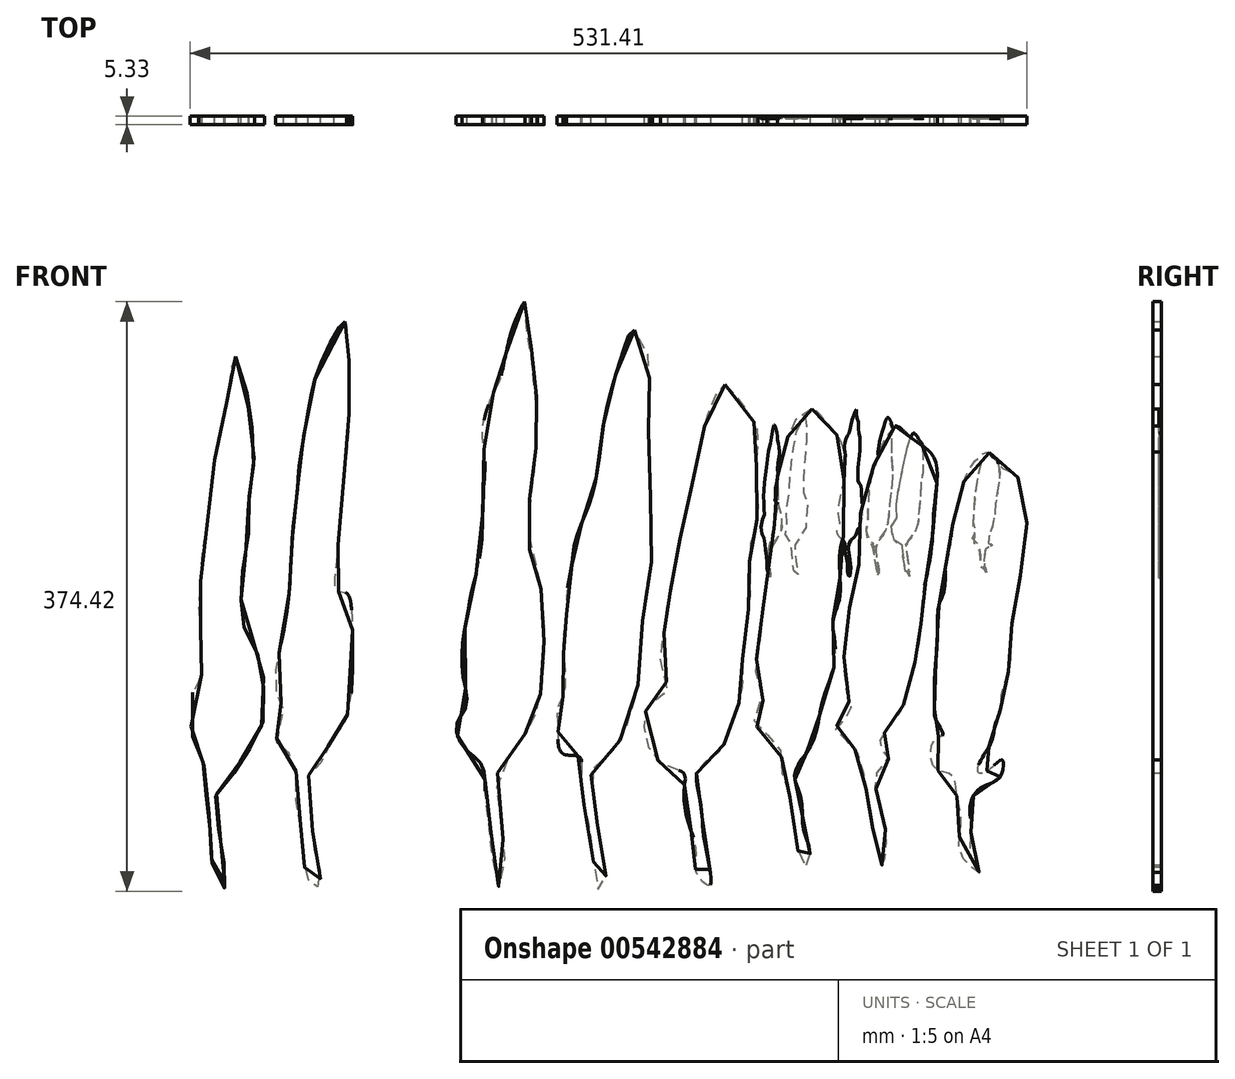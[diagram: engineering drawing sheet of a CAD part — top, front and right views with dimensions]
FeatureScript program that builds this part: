
annotation { "Feature Type Name" : "Feature", "Feature Type Description" : "" }
export const myFeature = defineFeature(function(context is Context, id is Id, definition is map)
    precondition{}
    {
        {
            var Q0;
            Q0=qCreatedBy(makeId("Front.planeOp"),FACE);
            var sketch = newSketch(context, id + "F0", { "sketchPlane" : qUnion([Q0])});
            skFitSpline(sketch, "E0", {"points": [v(-26.75, 46.41) * mm, v(-26.5, 43.12) * mm, v(-26, 39.07) * mm, v(-26, 32.23) * mm, v(-26.25, 24.64) * mm, v(-27.51, 13) * mm, v(-28.33, 2.5) * mm, v(-28.33, -2.36) * mm, v(-26.56, -2.8) * mm, v(-25.46, -7.65) * mm, v(-26.25, -24.73) * mm, v(-28.52, -28.78) * mm, v(-29.8, -30.55) * mm, v(-30.55, -33.08) * mm, v(-33.08, -35.36) * mm, v(-32.83, -41.7) * mm, v(-32.32, -49.5) * mm, v(-31.2, -54.37) * mm, v(-32.07, -56.37) * mm, v(-33.62, -54.37) * mm, v(-34.3, -49.5) * mm, v(-34.72, -45.33) * mm, v(-35.61, -40.17) * mm, v(-36.26, -32.55) * mm, v(-38.9, -30.55) * mm, v(-38.46, -26.6) * mm, v(-37.9, -23.97) * mm, v(-39.16, -20.94) * mm, v(-38.69, -13.6) * mm, v(-37.14, -5.44) * mm, v(-36.48, 4.03) * mm, v(-36.04, 9.98) * mm, v(-35.38, 15.94) * mm, v(-34.94, 21.22) * mm, v(-33.59, 29.2) * mm, v(-31.56, 37.8) * mm, v(-26.75, 46.41) * mm]});
            skFitSpline(sketch, "E1", {"points": [v(-8.5, 48.51) * mm, v(-7.65, 45.54) * mm, v(-7.65, 41.3) * mm, v(-7.65, 37.26) * mm, v(-7.86, 34.07) * mm, v(-8.29, 28.97) * mm, v(-8.71, 24.09) * mm, v(-9.35, 21.33) * mm, v(-9.14, 17.5) * mm, v(-9.77, 12.62) * mm, v(-8.71, 6.89) * mm, v(-7.65, 3.27) * mm, v(-7.44, -2.25) * mm, v(-6.8, -4.8) * mm, v(-6.8, -7.77) * mm, v(-7.22, -10.32) * mm, v(-7.86, -15) * mm, v(-8.29, -19.66) * mm, v(-9.99, -23.7) * mm, v(-11.47, -26.67) * mm, v(-12.32, -29.64) * mm, v(-15.08, -31.98) * mm, v(-16.14, -33.9) * mm, v(-16.14, -38.14) * mm, v(-15.72, -43.24) * mm, v(-15.08, -45.79) * mm, v(-14.45, -50.03) * mm, v(-14.02, -54.7) * mm, v(-14.66, -56.2) * mm, v(-15.72, -54.7) * mm, v(-16.36, -52.16) * mm, v(-16.78, -48.76) * mm, v(-17.63, -44.72) * mm, v(-18.06, -40.05) * mm, v(-18.48, -35.6) * mm, v(-19.33, -33.47) * mm, v(-22.1, -32.4) * mm, v(-23.58, -29.64) * mm, v(-23.15, -27.1) * mm, v(-22.1, -23.91) * mm, v(-22.1, -23.91) * mm, v(-21.24, -20.94) * mm, v(-22.1, -18.39) * mm, v(-22.73, -14.57) * mm, v(-22.73, -10.53) * mm, v(-22.1, -7.56) * mm, v(-21.67, -4.37) * mm, v(-21.45, 0) * mm, v(-21.03, 2.85) * mm, v(-20.18, 5.19) * mm, v(-18.48, 7.52) * mm, v(-18.48, 11.35) * mm, v(-17.84, 17.08) * mm, v(-17.2, 22.39) * mm, v(-16.57, 27.27) * mm, v(-15.72, 31.73) * mm, v(-14.87, 35.56) * mm, v(-13.6, 41.08) * mm, v(-11.68, 43.63) * mm, v(-10.4, 46.39) * mm, v(-8.5, 48.51) * mm]});
            skFitSpline(sketch, "E2", {"points": [v(-46.56, 40.04) * mm, v(-47.72, 35.4) * mm, v(-48.19, 31.7) * mm, v(-49.35, 26.59) * mm, v(-50.74, 18.7) * mm, v(-51.43, 11.74) * mm, v(-52.6, 5.25) * mm, v(-53.06, -1.94) * mm, v(-53.29, -5.88) * mm, v(-52.83, -10.3) * mm, v(-52.83, -14.47) * mm, v(-52.83, -17.95) * mm, v(-54.45, -21.2) * mm, v(-54.45, -28.59) * mm, v(-53.75, -30.24) * mm, v(-52.36, -33.95) * mm, v(-52.13, -37.66) * mm, v(-51.43, -42.53) * mm, v(-51.2, -46.47) * mm, v(-50.97, -50.65) * mm, v(-50.04, -54.82) * mm, v(-48.65, -56.45) * mm, v(-48.65, -54.13) * mm, v(-48.65, -51.58) * mm, v(-49.35, -47.63) * mm, v(-50.04, -43) * mm, v(-50.04, -39.28) * mm, v(-47.26, -36.5) * mm, v(-46.56, -34.65) * mm, v(-44.48, -31.86) * mm, v(-43.08, -29.08) * mm, v(-41.46, -25.83) * mm, v(-41.46, -21.89) * mm, v(-41.7, -16.55) * mm, v(-42.85, -13.07) * mm, v(-44.24, -9.6) * mm, v(-45.87, -8.44) * mm, v(-45.64, -4.72) * mm, v(-45.64, -1.7) * mm, v(-45.17, 2.23) * mm, v(-44.24, 7.57) * mm, v(-44.24, 11.98) * mm, v(-43.78, 17.77) * mm, v(-43.32, 20.33) * mm, v(-43.32, 25.43) * mm, v(-44.24, 30.53) * mm, v(-44.7, 35.17) * mm, v(-46.56, 40.04) * mm]});
            skFitSpline(sketch, "E3", {"points": [v(5.86, 50.01) * mm, v(5.86, 46.07) * mm, v(7.02, 42.13) * mm, v(7.02, 39.58) * mm, v(7.25, 35.87) * mm, v(8.18, 31.46) * mm, v(7.94, 27.52) * mm, v(7.94, 22.88) * mm, v(7.48, 18.47) * mm, v(6.78, 14.3) * mm, v(6.78, 9.89) * mm, v(6.78, 5.71) * mm, v(7.02, 3.63) * mm, v(8.4, 2.23) * mm, v(8.87, -2.4) * mm, v(9.33, -7.28) * mm, v(9.33, -11.22) * mm, v(9.33, -16.55) * mm, v(8.87, -20.03) * mm, v(7.94, -24.67) * mm, v(6.55, -26.3) * mm, v(5.86, -28.85) * mm, v(4.26, -31.3) * mm, v(1.32, -34.23) * mm, v(1.32, -43.58) * mm, v(1.94, -47.7) * mm, v(2.19, -52.4) * mm, v(1.32, -56.2) * mm, v(0, -52.4) * mm, v(0, -47.73) * mm, v(-1.22, -41.85) * mm, v(-1.35, -38.4) * mm, v(-1.95, -33.98) * mm, v(-5.05, -31) * mm, v(-6.5, -26.7) * mm, v(-4.8, -23.57) * mm, v(-5.22, -18.4) * mm, v(-5.45, -12.36) * mm, v(-4.55, -6.99) * mm, v(-3.66, -2.06) * mm, v(-2.54, 2.19) * mm, v(-1.87, 7.78) * mm, v(-1.62, 15.25) * mm, v(-1.37, 22.42) * mm, v(-1.8, 26.67) * mm, v(0, 33.06) * mm, v(1.32, 35.66) * mm, v(1.71, 37.09) * mm, v(2.38, 40.22) * mm, v(3.5, 44.7) * mm, v(5.86, 50.01) * mm]});
            skFitSpline(sketch, "E4", {"points": [v(-62.57, -56) * mm, v(-62.87, -50.88) * mm, v(-63.77, -44.86) * mm, v(-64.98, -39.44) * mm, v(-65.88, -34.31) * mm, v(-66.18, -27.38) * mm, v(-66.78, -19.55) * mm, v(-66.48, -14.73) * mm, v(-66.18, -8.1) * mm, v(-65.58, -2.37) * mm, v(-64.67, 3.95) * mm, v(-63.47, 10.58) * mm, v(-62.26, 15.1) * mm, v(-60.46, 18.72) * mm, v(-59.25, 15.1) * mm, v(-58.65, 10.28) * mm, v(-58.35, 2.75) * mm, v(-58.95, -3.28) * mm, v(-59.25, -10.2) * mm, v(-59.25, -15.63) * mm, v(-59.85, -19.55) * mm, v(-57.74, -24.37) * mm, v(-57.74, -28.59) * mm, v(-57.74, -28.59) * mm, v(-57.14, -34.31) * mm, v(-59.85, -38.83) * mm, v(-61.96, -42.75) * mm, v(-61.06, -51.19) * mm, v(-62.57, -56) * mm]});
            skFitSpline(sketch, "E5", {"points": [v(25.76, 44.9) * mm, v(23.67, 40.98) * mm, v(22.1, 35.74) * mm, v(20.52, 29.72) * mm, v(19.74, 24.48) * mm, v(18.95, 18.72) * mm, v(17.64, 13.49) * mm, v(16.07, 9.56) * mm, v(14.76, 5.37) * mm, v(14.5, 2.75) * mm, v(13.45, -3.27) * mm, v(13.45, -7.2) * mm, v(12.93, -10.34) * mm, v(12.93, -13.49) * mm, v(13.2, -17.94) * mm, v(12.93, -21.34) * mm, v(11.88, -23.44) * mm, v(11.88, -26.58) * mm, v(11.88, -29.46) * mm, v(12.93, -32.08) * mm, v(15.8, -32.6) * mm, v(16.07, -37.31) * mm, v(17.12, -43.34) * mm, v(18.17, -49.62) * mm, v(19.48, -56.95) * mm, v(20.52, -54.86) * mm, v(20, -50.4) * mm, v(18.95, -44.12) * mm, v(18.17, -38.1) * mm, v(18.17, -34.96) * mm, v(21.3, -32.08) * mm, v(24.19, -27.36) * mm, v(26.28, -20.3) * mm, v(27.07, -10.87) * mm, v(27.6, -4.58) * mm, v(28.9, 3.27) * mm, v(28.9, 10.87) * mm, v(28.38, 22.13) * mm, v(28.38, 28.67) * mm, v(28.38, 34.7) * mm, v(28.38, 39.93) * mm, v(25.76, 44.9) * mm]});
            skFitSpline(sketch, "E6", {"points": [v(42.26, 34.96) * mm, v(45.14, 31.55) * mm, v(48.02, 27.1) * mm, v(48.02, 23.17) * mm, v(48.02, 16.1) * mm, v(48.02, 10.34) * mm, v(46.7, 5.37) * mm, v(46.7, 2.23) * mm, v(46.7, -3.54) * mm, v(46.19, -7.72) * mm, v(45.4, -14.27) * mm, v(45.4, -18.98) * mm, v(44.61, -23.17) * mm, v(43.57, -26.32) * mm, v(41.2, -31.55) * mm, v(37.8, -34.17) * mm, v(37.02, -36.27) * mm, v(37.8, -41.24) * mm, v(38.33, -46.74) * mm, v(39.38, -52.5) * mm, v(39.38, -55.9) * mm, v(37.02, -53.55) * mm, v(37.02, -50.4) * mm, v(36.23, -46.48) * mm, v(34.93, -41.77) * mm, v(34.93, -37.31) * mm, v(34.66, -35.48) * mm, v(29.95, -33.12) * mm, v(27.6, -26.84) * mm, v(28.64, -22.91) * mm, v(31.78, -20.56) * mm, v(30.74, -16.63) * mm, v(31, -10.87) * mm, v(31.78, -5.1) * mm, v(32.3, -2.49) * mm, v(33.35, 3.27) * mm, v(34.66, 9.82) * mm, v(36.23, 16.89) * mm, v(38.07, 25.53) * mm, v(39.64, 31.03) * mm, v(42.26, 34.96) * mm]});
            skFitSpline(sketch, "E7", {"points": [v(90.18, 22.65) * mm, v(92.27, 20.03) * mm, v(95.15, 18.46) * mm, v(95.94, 14.8) * mm, v(96.99, 9.56) * mm, v(96.2, 3.54) * mm, v(95.41, -2.75) * mm, v(94.37, -7.72) * mm, v(94.1, -11.4) * mm, v(93.58, -17.41) * mm, v(92.27, -21.34) * mm, v(92.27, -23.7) * mm, v(91.22, -26.84) * mm, v(90.7, -29.46) * mm, v(88.08, -34.43) * mm, v(88.34, -35.48) * mm, v(90.7, -34.43) * mm, v(92.53, -33.12) * mm, v(92.27, -36) * mm, v(89.92, -37.58) * mm, v(88.08, -38.62) * mm, v(86.77, -40.98) * mm, v(86.77, -44.12) * mm, v(86.77, -47) * mm, v(87.03, -51.45) * mm, v(88.34, -53.55) * mm, v(85.17, -50.6) * mm, v(84.94, -45.96) * mm, v(84.94, -42.45) * mm, v(84.15, -38.62) * mm, v(83.63, -36) * mm, v(80.75, -34.96) * mm, v(79.44, -32.08) * mm, v(80.75, -28.94) * mm, v(81.8, -28.67) * mm, v(80.49, -25.8) * mm, v(80.23, -23.2) * mm, v(80.23, -17.94) * mm, v(80.75, -11.91) * mm, v(81.01, -5.1) * mm, v(82.06, -2.23) * mm, v(82.32, 2.49) * mm, v(83.37, 6.68) * mm, v(83.63, 9.82) * mm, v(84.68, 13.75) * mm, v(85.73, 17.94) * mm, v(88.08, 21.6) * mm, v(90.18, 22.65) * mm]});
            skFitSpline(sketch, "E8", {"points": [v(57.98, 30.54) * mm, v(54.5, 27.83) * mm, v(53.34, 23.96) * mm, v(51.8, 18.55) * mm, v(51.8, 12.37) * mm, v(49.86, 4.25) * mm, v(50.25, 1.93) * mm, v(49.47, -2.32) * mm, v(48.7, -10.44) * mm, v(47.93, -18.55) * mm, v(49.09, -22.42) * mm, v(47.93, -23.58) * mm, v(47.93, -27.06) * mm, v(51.8, -30.15) * mm, v(52.57, -35.56) * mm, v(54.11, -40.2) * mm, v(55.27, -49.09) * mm, v(57.2, -52.57) * mm, v(57.6, -49.47) * mm, v(56.43, -45.6) * mm, v(56.04, -40.2) * mm, v(54.88, -36.72) * mm, v(55.27, -34.4) * mm, v(56.82, -32.08) * mm, v(58.75, -28.22) * mm, v(59.9, -22.42) * mm, v(62.23, -14.69) * mm, v(61.84, -7.72) * mm, v(63, -3.87) * mm, v(63, 3.87) * mm, v(63.77, 8.5) * mm, v(63.77, 17.78) * mm, v(63.39, 24.35) * mm, v(59.9, 28.99) * mm, v(57.98, 30.54) * mm]});
            skFitSpline(sketch, "E9", {"points": [v(73.05, 27.44) * mm, v(69.57, 21.26) * mm, v(66.87, 11.98) * mm, v(66.48, 2.32) * mm, v(64.93, -5.02) * mm, v(63.77, -13.91) * mm, v(64.55, -22.03) * mm, v(64.93, -24.74) * mm, v(62.23, -27.44) * mm, v(64.93, -30.15) * mm, v(67.25, -35.17) * mm, v(68.41, -42.13) * mm, v(69.57, -48.32) * mm, v(70.73, -52.18) * mm, v(71.5, -47.54) * mm, v(70.35, -41.74) * mm, v(69.96, -35.17) * mm, v(71.9, -32.85) * mm, v(70.35, -30.54) * mm, v(72.66, -26.28) * mm, v(74.6, -23.2) * mm, v(76.53, -16.23) * mm, v(77.69, -10.44) * mm, v(78.08, -3.87) * mm, v(79.62, 4.64) * mm, v(80.23, 13.14) * mm, v(80.23, 21.65) * mm, v(75.76, 25.51) * mm, v(73.05, 27.44) * mm]});
            skSolve(sketch);
        }
        {
            var Q0;
            Q0=qSketchRegion(id+"F0",true);
            extrude(context, id + "F1", {"entities" : qUnion([Q0]), "depth" : 1.52 * mm, "offsetDistance" : 25.4 * mm});
        }
        {
            var Q0;
            Q0=makeQuery(id+"F1.opExtrude","SWEPT_BODY",BODY,{"disambiguationData":[OSD([sQuery(id+"F0.wireOp",EDGE,"E4")])]});
            var Q1;
            Q1=makeQuery(id+"F1.opExtrude","SWEPT_BODY",BODY,{"disambiguationData":[OSD([sQuery(id+"F0.wireOp",EDGE,"E2")])]});
            var Q2;
            Q2=makeQuery(id+"F1.opExtrude","SWEPT_BODY",BODY,{"disambiguationData":[OSD([sQuery(id+"F0.wireOp",EDGE,"E1")])]});
            var Q3;
            Q3=makeQuery(id+"F1.opExtrude","SWEPT_BODY",BODY,{"disambiguationData":[OSD([sQuery(id+"F0.wireOp",EDGE,"E0")])]});
            var Q4;
            Q4=makeQuery(id+"F1.opExtrude","SWEPT_BODY",BODY,{"disambiguationData":[OSD([sQuery(id+"F0.wireOp",EDGE,"E3")])]});
            var Q5;
            Q5=makeQuery(id+"F1.opExtrude","SWEPT_BODY",BODY,{"disambiguationData":[OSD([sQuery(id+"F0.wireOp",EDGE,"E5")])]});
            var Q6;
            Q6=makeQuery(id+"F1.opExtrude","SWEPT_BODY",BODY,{"disambiguationData":[OSD([sQuery(id+"F0.wireOp",EDGE,"E6")])]});
            var Q7;
            Q7=makeQuery(id+"F1.opExtrude","SWEPT_BODY",BODY,{"disambiguationData":[OSD([sQuery(id+"F0.wireOp",EDGE,"E8")])]});
            var Q8;
            Q8=makeQuery(id+"F1.opExtrude","SWEPT_BODY",BODY,{"disambiguationData":[OSD([sQuery(id+"F0.wireOp",EDGE,"E9")])]});
            var Q9;
            Q9=makeQuery(id+"F1.opExtrude","SWEPT_BODY",BODY,{"disambiguationData":[OSD([sQuery(id+"F0.wireOp",EDGE,"E7")])]});
            var Q10;
            Q10=sQuery(id+"F0.wireOp",VERTEX,"E7.0.internal");
            transform(context, id + "F2", {"entities" : qUnion([Q0, Q1, Q2, Q3, Q4, Q5, Q6, Q7, Q8, Q9]), "transformType" : TransformType.SCALE_UNIFORMLY, "scale" : 3.5, "scalePoint" : qUnion([Q10]), "makeCopy" : false});
        }
        {
            var Q0;
            Q0=makeQuery(id+"F1.opExtrude","CAP_FACE",FACE,{"disambiguationData":[OSD([sQuery(id+"F0.wireOp",EDGE,"E4")])],"isStart":false});
            var sketch = newSketch(context, id + "F3", { "sketchPlane" : qUnion([Q0])});
            skPoint(sketch, "E10", {"position": v(87.01, 21.31) * mm});
            skPoint(sketch, "E11", {"position": v(82.1, -244.62) * mm});
            skPoint(sketch, "E12", {"position": v(64.9, -40.1) * mm});
            skPoint(sketch, "E13", {"position": v(112.8, -26.6) * mm});
            skSolve(sketch);
        }
        {
            var Q0;
            Q0=makeQuery(id+"F0.imprint","IMPRINT",FACE,{"disambiguationData":[TD([[makeQuery(id+"F0.imprint","IMPRINT",EDGE,{"derivedFrom":sQuery(id+"F0.wireOp",EDGE,"E4")}),-1.0]])]});
            var Q1;
            Q1=makeQuery(id+"F0.imprint","IMPRINT",FACE,{"disambiguationData":[TD([[makeQuery(id+"F0.imprint","IMPRINT",EDGE,{"derivedFrom":sQuery(id+"F0.wireOp",EDGE,"E2")}),1.0]])]});
            var Q2;
            Q2=makeQuery(id+"F0.imprint","IMPRINT",FACE,{"disambiguationData":[TD([[makeQuery(id+"F0.imprint","IMPRINT",EDGE,{"derivedFrom":sQuery(id+"F0.wireOp",EDGE,"E0")}),-1.0]])]});
            var Q3;
            Q3=makeQuery(id+"F0.imprint","IMPRINT",FACE,{"disambiguationData":[TD([[makeQuery(id+"F0.imprint","IMPRINT",EDGE,{"derivedFrom":sQuery(id+"F0.wireOp",EDGE,"E1")}),-1.0]])]});
            var Q4;
            Q4=makeQuery(id+"F0.imprint","IMPRINT",FACE,{"disambiguationData":[TD([[makeQuery(id+"F0.imprint","IMPRINT",EDGE,{"derivedFrom":sQuery(id+"F0.wireOp",EDGE,"E3")}),-1.0]])]});
            var Q5;
            Q5=makeQuery(id+"F0.imprint","IMPRINT",FACE,{"disambiguationData":[TD([[makeQuery(id+"F0.imprint","IMPRINT",EDGE,{"derivedFrom":sQuery(id+"F0.wireOp",EDGE,"E5")}),1.0]])]});
            var Q6;
            Q6=makeQuery(id+"F0.imprint","IMPRINT",FACE,{"disambiguationData":[TD([[makeQuery(id+"F0.imprint","IMPRINT",EDGE,{"derivedFrom":sQuery(id+"F0.wireOp",EDGE,"E6")}),-1.0]])]});
            var Q7;
            Q7=makeQuery(id+"F0.imprint","IMPRINT",FACE,{"disambiguationData":[TD([[makeQuery(id+"F0.imprint","IMPRINT",EDGE,{"derivedFrom":sQuery(id+"F0.wireOp",EDGE,"E7")}),-1.0]])]});
            extrude(context, id + "F4", {"entities" : qUnion([Q0, Q1, Q2, Q3, Q4, Q5, Q6, Q7]), "depth" : 1.52 * mm, "offsetDistance" : 25.4 * mm});
        }
    });
